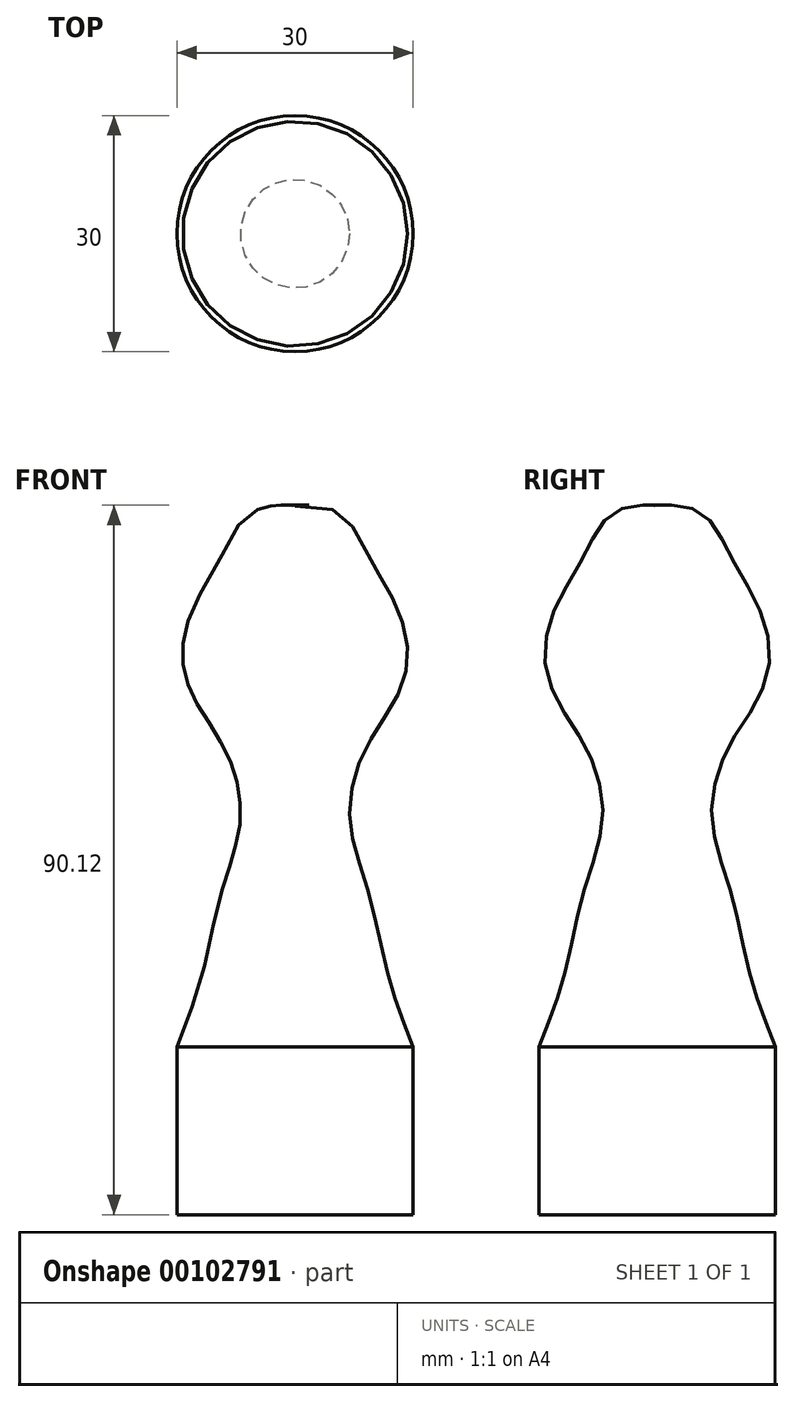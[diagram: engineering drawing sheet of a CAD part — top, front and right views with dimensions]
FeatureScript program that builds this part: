
annotation { "Feature Type Name" : "Feature", "Feature Type Description" : "" }
export const myFeature = defineFeature(function(context is Context, id is Id, definition is map)
    precondition{}
    {
        {
            var Q0;
            Q0=qCreatedBy(makeId("Front.planeOp"),FACE);
            var sketch = newSketch(context, id + "F0", { "sketchPlane" : qUnion([Q0])});
            skLineSegment(sketch, "E0", {"start": v(15, -43.43) * mm, "end": v(15, -22.14) * mm});
            skFitSpline(sketch, "E1", {"points": [v(0, 46.57) * mm, v(8.97, 40.95) * mm, v(13.6, 31.98) * mm, v(13.6, 23.87) * mm, v(8.97, 15.77) * mm, v(6.94, 6.8) * mm, v(9.26, -2.17) * mm, v(11.86, -13.17) * mm, v(15, -22.14) * mm], "startDerivative": vector(144, 18.49) * mm, "endDerivative": vector(27.35, -69.37) * mm});
            skLineSegment(sketch, "E2", {"start": v(15, -43.43) * mm, "end": v(0, -43.43) * mm});
            skLineSegment(sketch, "E3", {"start": v(0, 46.57) * mm, "end": v(0, -43.43) * mm});
            skSolve(sketch);
        }
        {
            var Q0;
            Q0=makeQuery(id+"F0.imprint","IMPRINT",FACE,{"disambiguationData":[TD([[makeQuery(id+"F0.imprint","IMPRINT",EDGE,{"derivedFrom":sQuery(id+"F0.wireOp",EDGE,"E0")}),1.0]])]});
            var Q1;
            Q1=sQuery(id+"F0.wireOp",EDGE,"E3");
            revolve(context, id + "F1", {"entities" : qUnion([Q0]), "axis" : qUnion([Q1]), "revolveType" : RevolveType.FULL});
        }
    });
